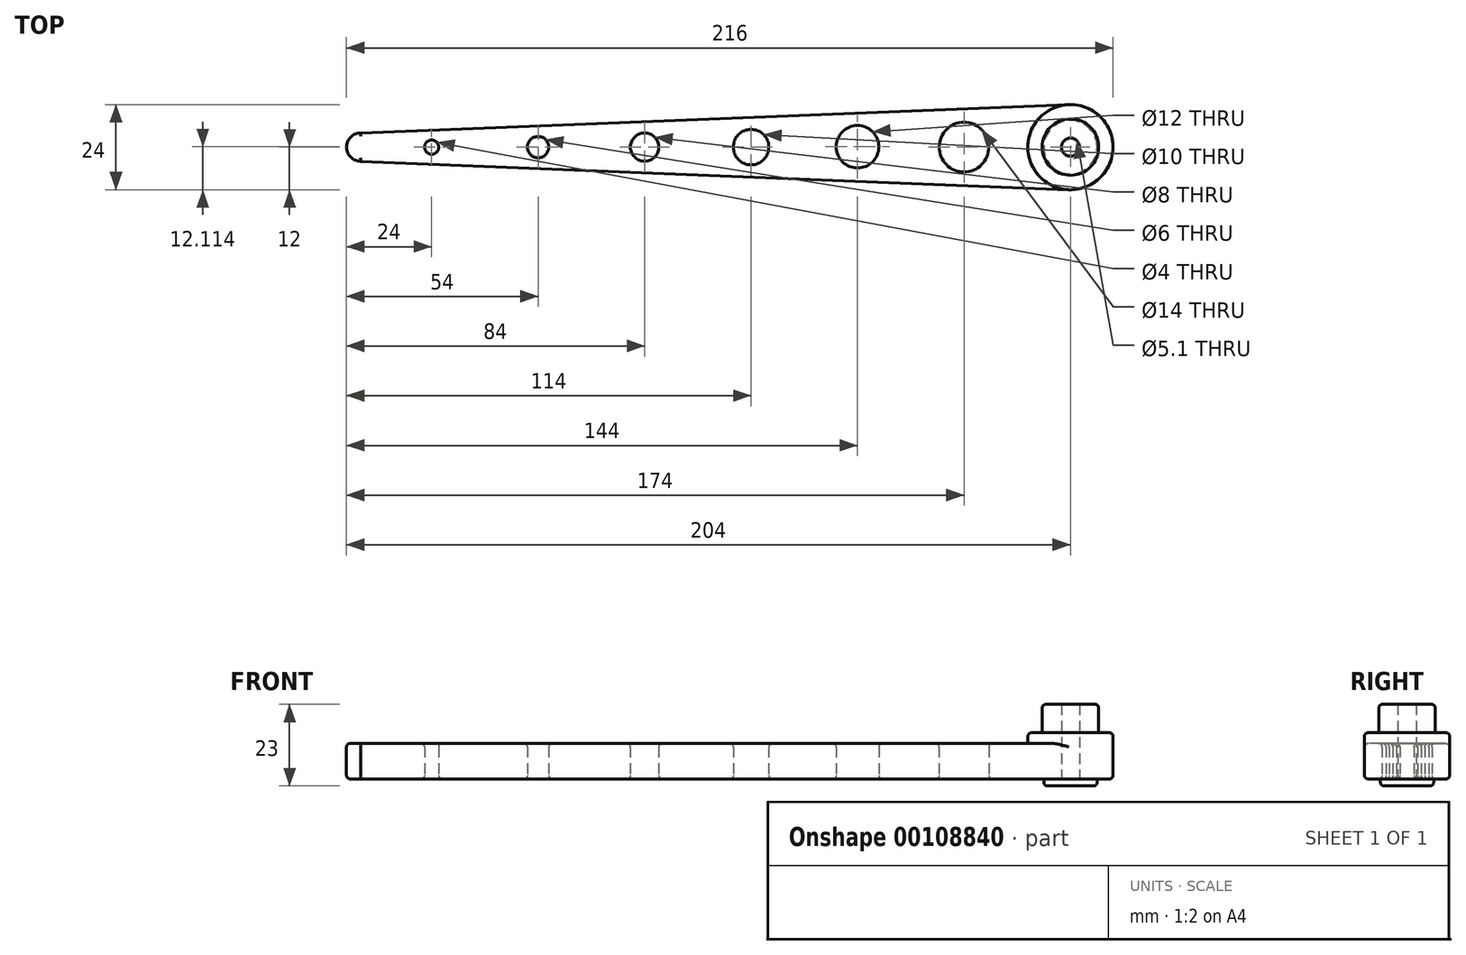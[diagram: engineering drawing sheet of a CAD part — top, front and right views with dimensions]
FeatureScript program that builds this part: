
annotation { "Feature Type Name" : "Feature", "Feature Type Description" : "" }
export const myFeature = defineFeature(function(context is Context, id is Id, definition is map)
    precondition{}
    {
        {
            var Q0;
            Q0=qCreatedBy(makeId("Top.planeOp"),FACE);
            var sketch = newSketch(context, id + "F0", { "sketchPlane" : qUnion([Q0])});
            skLineSegment(sketch, "E0", {"start": v(43.95, 0) * mm, "end": v(-214.48, 0) * mm, "construction": true});
            skLineSegment(sketch, "E1", {"start": v(0, 32.9) * mm, "end": v(0, -28.9) * mm, "construction": true});
            skLineSegment(sketch, "E2", {"start": v(-200, 16.62) * mm, "end": v(-200, -19.58) * mm, "construction": true});
            skCircle(sketch, "E3", {"center": v(0, 0) * mm, "radius": 2.55 * mm});
            skCircle(sketch, "E4", {"center": v(0, 0) * mm, "radius": 12 * mm});
            skCircle(sketch, "E5", {"center": v(-200, 0) * mm, "radius": 4 * mm});
            skLineSegment(sketch, "E6", {"start": v(-200, 4) * mm, "end": v(0, 12) * mm});
            skLineSegment(sketch, "E7", {"start": v(-200, -4) * mm, "end": v(0, -12) * mm});
            skCircle(sketch, "E8", {"center": v(0, 0) * mm, "radius": 7.95 * mm});
            skCircle(sketch, "E9", {"center": v(0, 0) * mm, "radius": 7.5 * mm});
            skLineSegment(sketch, "E10", {"start": v(-30, 21.22) * mm, "end": v(-30, -28.67) * mm, "construction": true});
            skLineSegment(sketch, "E11", {"start": v(-60, 20.5) * mm, "end": v(-60, -20.27) * mm, "construction": true});
            skLineSegment(sketch, "E12", {"start": v(-90, 22.66) * mm, "end": v(-90, -20.27) * mm, "construction": true});
            skLineSegment(sketch, "E13", {"start": v(-120, 17.38) * mm, "end": v(-120, -20.27) * mm, "construction": true});
            skCircle(sketch, "E14", {"center": v(-30, 0) * mm, "radius": 7 * mm});
            skCircle(sketch, "E15", {"center": v(-60, 0.11) * mm, "radius": 6 * mm});
            skCircle(sketch, "E16", {"center": v(-90, 0) * mm, "radius": 5 * mm});
            skCircle(sketch, "E17", {"center": v(-120, 0) * mm, "radius": 4 * mm});
            skLineSegment(sketch, "E18", {"start": v(-150, 17.3) * mm, "end": v(-150, -21.42) * mm, "construction": true});
            skLineSegment(sketch, "E19", {"start": v(-180, 18.04) * mm, "end": v(-180, -17.3) * mm, "construction": true});
            skCircle(sketch, "E20", {"center": v(-150, 0) * mm, "radius": 3 * mm});
            skCircle(sketch, "E21", {"center": v(-180, 0) * mm, "radius": 2 * mm});
            skSolve(sketch);
        }
        {
            var Q0;
            {var subQ0=sQuery(id+"F0.wireOp",EDGE,"E5");var subQ1=makeQuery(id+"F0.imprint","INTERSECT",VERTEX,{"derivedFrom":[subQ0,sQuery(id+"F0.wireOp",EDGE,"E6")]});Q0=makeQuery(id+"F0.imprint","IMPRINT",FACE,{"disambiguationData":[TD([[makeQuery(id+"F0.imprint","IMPRINT",EDGE,{"disambiguationData":[TD([[subQ1,-1.0]])],"derivedFrom":subQ0}),1.0]])]});}
            var Q1;
            {var subQ0=sQuery(id+"F0.wireOp",EDGE,"E6");var subQ1=sQuery(id+"F0.wireOp",EDGE,"E4");var subQ2=makeQuery(id+"F0.imprint","INTERSECT",VERTEX,{"derivedFrom":[subQ1,subQ0]});Q1=makeQuery(id+"F0.imprint","IMPRINT",FACE,{"disambiguationData":[TD([[makeQuery(id+"F0.imprint","IMPRINT",EDGE,{"disambiguationData":[TD([[subQ2,-1.0]])],"derivedFrom":subQ1}),-1.0]])]});}
            extrude(context, id + "F1", {"entities" : qUnion([Q0, Q1]), "depth" : 10 * mm});
        }
        {
            var Q0;
            Q0=makeQuery(id+"F0.imprint","IMPRINT",FACE,{"disambiguationData":[TD([[makeQuery(id+"F0.imprint","IMPRINT",EDGE,{"derivedFrom":sQuery(id+"F0.wireOp",EDGE,"E8")}),-1.0]])]});
            extrude(context, id + "F2", {"entities" : qUnion([Q0]), "operationType" : NewBodyOperationType.ADD, "depth" : 13 * mm});
        }
        {
            var Q0;
            Q0=makeQuery(id+"F0.imprint","IMPRINT",FACE,{"disambiguationData":[TD([[makeQuery(id+"F0.imprint","IMPRINT",EDGE,{"derivedFrom":sQuery(id+"F0.wireOp",EDGE,"E8")}),1.0]])]});
            var Q1;
            Q1=makeQuery(id+"F0.imprint","IMPRINT",FACE,{"disambiguationData":[TD([[makeQuery(id+"F0.imprint","IMPRINT",EDGE,{"derivedFrom":sQuery(id+"F0.wireOp",EDGE,"E3")}),-1.0]])]});
            extrude(context, id + "F3", {"entities" : qUnion([Q0, Q1]), "operationType" : NewBodyOperationType.ADD, "depth" : 21 * mm});
        }
        {
            var Q0;
            Q0=makeQuery(id+"F0.imprint","IMPRINT",FACE,{"disambiguationData":[TD([[makeQuery(id+"F0.imprint","IMPRINT",EDGE,{"derivedFrom":sQuery(id+"F0.wireOp",EDGE,"E3")}),-1.0]])]});
            extrude(context, id + "F4", {"entities" : qUnion([Q0]), "operationType" : NewBodyOperationType.ADD, "oppositeDirection" : true, "depth" : 2 * mm});
        }
        {
            var Q0;
            Q0=makeQuery(id+"F1.opExtrude","CAP_EDGE",EDGE,{"disambiguationData":[OSD([sQuery(id+"F0.wireOp",EDGE,"E6")])],"isStart":false});
            var Q1;
            Q1=makeQuery(id+"F1.opExtrude","CAP_EDGE",EDGE,{"disambiguationData":[OSD([sQuery(id+"F0.wireOp",EDGE,"E5")])],"isStart":false});
            var Q2;
            Q2=makeQuery(id+"F1.opExtrude","CAP_EDGE",EDGE,{"disambiguationData":[OSD([sQuery(id+"F0.wireOp",EDGE,"E7")])],"isStart":false});
            var Q3;
            Q3=makeQuery(id+"F2.opExtrude","CAP_EDGE",EDGE,{"disambiguationData":[OSD([sQuery(id+"F0.wireOp",EDGE,"E4")])],"isStart":false});
            var Q4;
            Q4=makeQuery(id+"F3.opExtrude","CAP_EDGE",EDGE,{"disambiguationData":[OSD([sQuery(id+"F0.wireOp",EDGE,"E8")])],"isStart":false});
            var Q5;
            Q5=makeQuery(id+"F1.opExtrude","CAP_EDGE",EDGE,{"disambiguationData":[OSD([sQuery(id+"F0.wireOp",EDGE,"E6")])],"isStart":true});
            var Q6;
            Q6=makeQuery(id+"F2.opExtrude","CAP_EDGE",EDGE,{"disambiguationData":[OSD([sQuery(id+"F0.wireOp",EDGE,"E4")])],"isStart":true});
            var Q7;
            Q7=makeQuery(id+"F1.opExtrude","CAP_EDGE",EDGE,{"disambiguationData":[OSD([sQuery(id+"F0.wireOp",EDGE,"E7")])],"isStart":true});
            var Q8;
            Q8=makeQuery(id+"F1.opExtrude","CAP_EDGE",EDGE,{"disambiguationData":[OSD([sQuery(id+"F0.wireOp",EDGE,"E5")])],"isStart":true});
            var Q9;
            Q9=makeQuery(id+"F4.opExtrude","CAP_EDGE",EDGE,{"disambiguationData":[OSD([sQuery(id+"F0.wireOp",EDGE,"E9")])],"isStart":false});
            var Q10;
            Q10=makeQuery(id+"F1.opExtrude","CAP_EDGE",EDGE,{"disambiguationData":[OSD([sQuery(id+"F0.wireOp",EDGE,"E14")])],"isStart":true});
            var Q11;
            Q11=makeQuery(id+"F1.opExtrude","CAP_EDGE",EDGE,{"disambiguationData":[OSD([sQuery(id+"F0.wireOp",EDGE,"E15")])],"isStart":true});
            var Q12;
            Q12=makeQuery(id+"F1.opExtrude","CAP_EDGE",EDGE,{"disambiguationData":[OSD([sQuery(id+"F0.wireOp",EDGE,"E16")])],"isStart":true});
            var Q13;
            Q13=makeQuery(id+"F1.opExtrude","CAP_EDGE",EDGE,{"disambiguationData":[OSD([sQuery(id+"F0.wireOp",EDGE,"E17")])],"isStart":true});
            fillet(context, id + "F5", {"entities" : qUnion([Q0, Q1, Q2, Q3, Q4, Q5, Q6, Q7, Q8, Q9, Q10, Q11, Q12, Q13]), "radius" : 1 * mm, "tangentPropagation" : true, "allowEdgeOverflow" : false});
        }
        {
            var Q0;
            Q0=makeQuery(id+"F1.opExtrude","CAP_EDGE",EDGE,{"disambiguationData":[OSD([sQuery(id+"F0.wireOp",EDGE,"E14")])],"isStart":false});
            var Q1;
            {var subQ0=sQuery(id+"F0.wireOp",EDGE,"E15");Q1=makeQuery(id+"F5.opFillet","BLEND_EDGE",EDGE,{"blendedFrom":[makeQuery(id+"F1.opExtrude","CAP_EDGE",EDGE,{"disambiguationData":[OSD([subQ0])],"isStart":true}),makeQuery(id+"F1.opExtrude","SWEPT_FACE",FACE,{"disambiguationData":[OSD([subQ0])]})],"blendedInto":[makeQuery(id+"F1.opExtrude","SWEPT_FACE",FACE,{"disambiguationData":[OSD([subQ0])]})]});}
            var Q2;
            Q2=makeQuery(id+"F1.opExtrude","CAP_EDGE",EDGE,{"disambiguationData":[OSD([sQuery(id+"F0.wireOp",EDGE,"E16")])],"isStart":false});
            var Q3;
            Q3=makeQuery(id+"F1.opExtrude","CAP_EDGE",EDGE,{"disambiguationData":[OSD([sQuery(id+"F0.wireOp",EDGE,"E17")])],"isStart":false});
            var Q4;
            Q4=makeQuery(id+"F1.opExtrude","CAP_EDGE",EDGE,{"disambiguationData":[OSD([sQuery(id+"F0.wireOp",EDGE,"E15")])],"isStart":false});
            var Q5;
            Q5=makeQuery(id+"F1.opExtrude","CAP_EDGE",EDGE,{"disambiguationData":[OSD([sQuery(id+"F0.wireOp",EDGE,"E20")])],"isStart":false});
            var Q6;
            Q6=makeQuery(id+"F1.opExtrude","CAP_EDGE",EDGE,{"disambiguationData":[OSD([sQuery(id+"F0.wireOp",EDGE,"E21")])],"isStart":false});
            var Q7;
            Q7=makeQuery(id+"F1.opExtrude","CAP_EDGE",EDGE,{"disambiguationData":[OSD([sQuery(id+"F0.wireOp",EDGE,"E20")])],"isStart":true});
            var Q8;
            Q8=makeQuery(id+"F1.opExtrude","CAP_EDGE",EDGE,{"disambiguationData":[OSD([sQuery(id+"F0.wireOp",EDGE,"E21")])],"isStart":true});
            fillet(context, id + "F6", {"entities" : qUnion([Q0, Q1, Q2, Q3, Q4, Q5, Q6, Q7, Q8]), "radius" : 1 * mm, "tangentPropagation" : true, "allowEdgeOverflow" : false});
        }
    });
